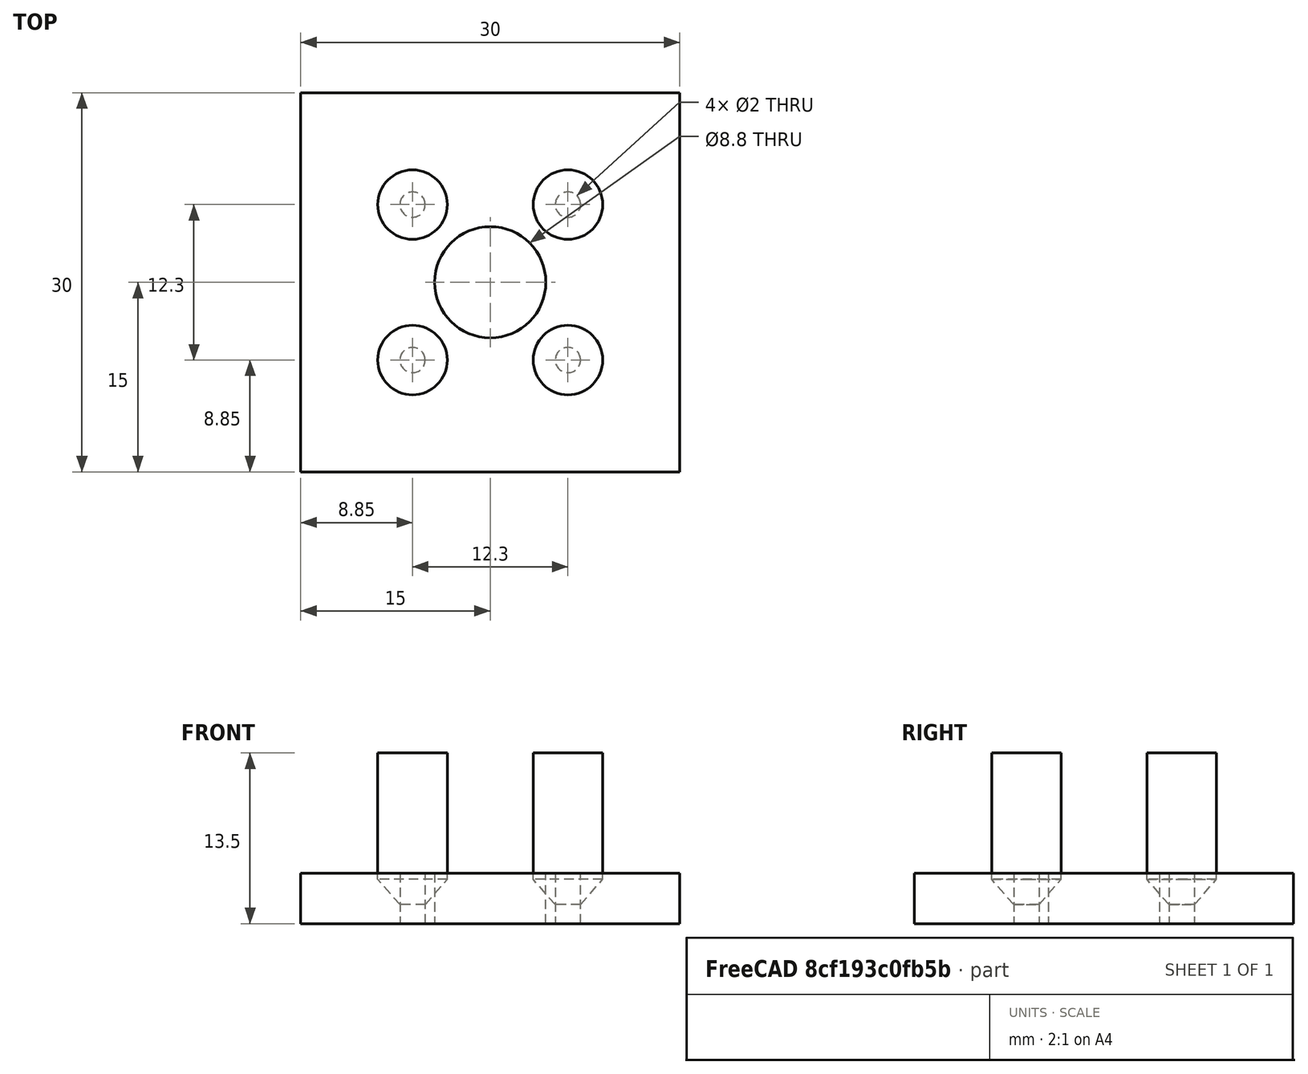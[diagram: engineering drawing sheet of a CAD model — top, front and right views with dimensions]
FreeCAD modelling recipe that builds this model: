
FCSTD DOCUMENT  (FreeCAD 0.19R0.19.2)
Label: motorMount004
License: All rights reserved
LicenseURL: http://en.wikipedia.org/wiki/All_rights_reserved
objects: Part::Cone×4, Part::Cylinder×4, Part::Fuse×4, Sketcher::SketchObject×1, Part::Extrusion×1, Part::MultiFuse×1
note: 15 computed .brp shape members not serialized (recipe doc carries the construction recipe); baked Part::Feature solids carry a one-line shape summary decoded from their .brp

FEATURE [Sketcher::SketchObject] Sketch
  FullyConstrained = true
  sketch-geometry (9):
    g0: Circle CenterX=6.15 CenterY=6.15 CenterZ=0 NormalX=0 NormalY=0 NormalZ=1 AngleXU=0 Radius=4.4
    g1: LineSegment StartX=-8.85 StartY=21.15 StartZ=0 EndX=21.15 EndY=21.15 EndZ=0
    g2: LineSegment StartX=21.15 StartY=21.15 StartZ=0 EndX=21.15 EndY=-8.85 EndZ=0
    g3: LineSegment StartX=-8.85 StartY=21.15 StartZ=0 EndX=-8.85 EndY=-8.85 EndZ=0
    g4: LineSegment StartX=-8.85 StartY=-8.85 StartZ=0 EndX=21.15 EndY=-8.85 EndZ=0
    g5: Circle CenterX=0 CenterY=12.3 CenterZ=0 NormalX=0 NormalY=0 NormalZ=1 AngleXU=0 Radius=1
    g6: Circle CenterX=12.3 CenterY=12.3 CenterZ=0 NormalX=0 NormalY=0 NormalZ=1 AngleXU=0 Radius=1
    g7: Circle CenterX=12.3 CenterY=0 CenterZ=0 NormalX=0 NormalY=0 NormalZ=1 AngleXU=0 Radius=1
    g8: Circle CenterX=0 CenterY=0 CenterZ=0 NormalX=0 NormalY=0 NormalZ=1 AngleXU=0 Radius=1
  constraints (18):
    c: Block(g0)
    c: Horizontal(g1)
    c: Distance(g1) = 30
    c: Vertical(g2)
    c: Block(g1)
    c: Distance(g2) = 30
    c: Coincident(g2,g1)
    c: Vertical(g3)
    c: Distance(g3) = 30
    c: Coincident(g3,g1)
    c: Block(g3)
    c: Block(g2)
    c: Coincident(g4,g3)
    c: Coincident(g4,g2)
    c: Block(g5)
    c: Block(g6)
    c: Block(g7)
    c: Block(g8)
FEATURE [Part::Extrusion] Extrude
  Base = -> Sketch
  Dir = (0,0,1)
  DirMode = 2
  FaceMakerClass = Part::FaceMakerBullseye
  LengthFwd = 4
  LengthRev = 0
  Solid = true
  Symmetric = false
FEATURE [Part::Cone] Cone
  Angle = 360
  AttacherType = Attacher::AttachEngine3D
  Height = 2
  Placement = pos=(0,0,1.5) rot=(0,0,1;0rad)
  Radius1 = 1
  Radius2 = 2.75
FEATURE [Part::Cylinder] Cylinder
  Angle = 360
  AttacherType = Attacher::AttachEngine3D
  Height = 10
  Placement = pos=(0,0,3.5) rot=(0,0,1;0rad)
  Radius = 2.75
FEATURE [Part::Fuse] Fusion  label="removeFromMainToCreateScrewChamfer"
  Base = -> Cone
  Tool = -> Cylinder
FEATURE [Part::Cone] Cone001
  Angle = 360
  AttacherType = Attacher::AttachEngine3D
  Height = 2
  Placement = pos=(0,0,1.5) rot=(0,0,1;0rad)
  Radius1 = 1
  Radius2 = 2.75
FEATURE [Part::Cylinder] Cylinder001
  Angle = 360
  AttacherType = Attacher::AttachEngine3D
  Height = 10
  Placement = pos=(0,0,3.5) rot=(0,0,1;0rad)
  Radius = 2.75
FEATURE [Part::Fuse] Fusion001  label="removeFromMainToCreateScrewChamfer001"
  Base = -> Cone001
  Placement = pos=(12.3,0,0) rot=(0,0,1;0rad)
  Tool = -> Cylinder001
FEATURE [Part::Cone] Cone002
  Angle = 360
  AttacherType = Attacher::AttachEngine3D
  Height = 2
  Placement = pos=(0,0,1.5) rot=(0,0,1;0rad)
  Radius1 = 1
  Radius2 = 2.75
FEATURE [Part::Cylinder] Cylinder002
  Angle = 360
  AttacherType = Attacher::AttachEngine3D
  Height = 10
  Placement = pos=(0,0,3.5) rot=(0,0,1;0rad)
  Radius = 2.75
FEATURE [Part::Fuse] Fusion002  label="removeFromMainToCreateScrewChamfer002"
  Base = -> Cone002
  Placement = pos=(12.3,12.3,0) rot=(0,0,1;0rad)
  Tool = -> Cylinder002
FEATURE [Part::Cone] Cone003
  Angle = 360
  AttacherType = Attacher::AttachEngine3D
  Height = 2
  Placement = pos=(0,0,1.5) rot=(0,0,1;0rad)
  Radius1 = 1
  Radius2 = 2.75
FEATURE [Part::Cylinder] Cylinder003
  Angle = 360
  AttacherType = Attacher::AttachEngine3D
  Height = 10
  Placement = pos=(0,0,3.5) rot=(0,0,1;0rad)
  Radius = 2.75
FEATURE [Part::Fuse] Fusion003  label="removeFromMainToCreateScrewChamfer003"
  Base = -> Cone003
  Placement = pos=(0,12.3,0) rot=(0,0,1;0rad)
  Tool = -> Cylinder003
FEATURE [Part::MultiFuse] Fusion004  label="removeFromMainToCreateScrewChamfer004"
  Shapes = -> [Fusion,Fusion001,Fusion002,Fusion003]
